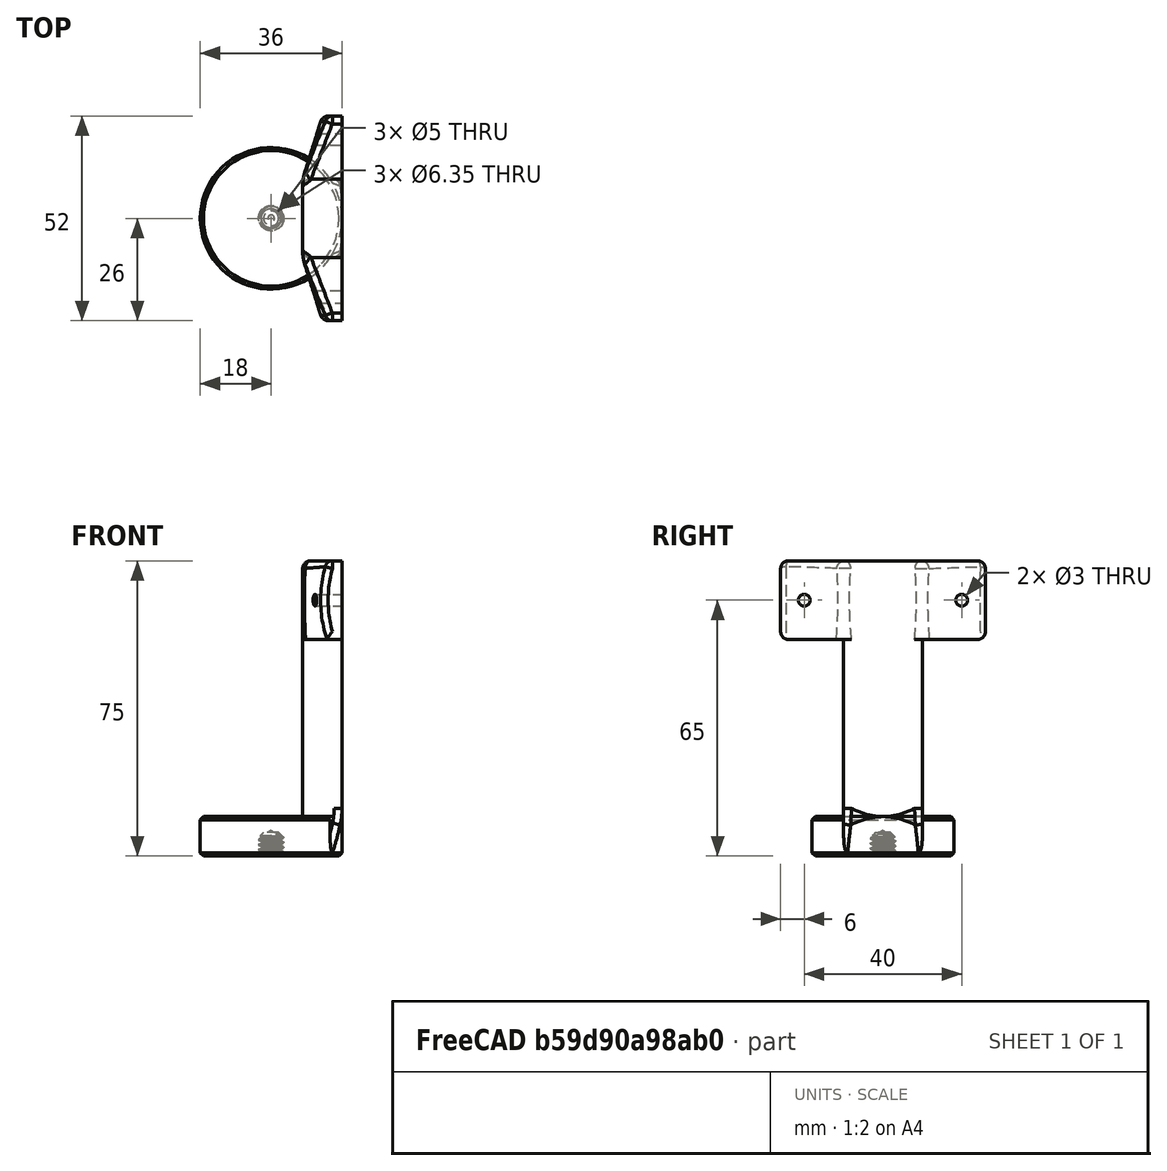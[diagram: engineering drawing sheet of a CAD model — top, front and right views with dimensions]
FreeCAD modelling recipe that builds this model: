
FCSTD DOCUMENT  (FreeCAD 0.21R33668 +7 (Git))
Label: _RaspiCam-Holder
License: Creative Commons Attribution 4.0
LicenseURL: https://creativecommons.org/licenses/by/4.0/
objects: Sketcher::SketchObject×7, PartDesign::Fillet×3, PartDesign::AdditiveLoft×2, PartDesign::Revolution×1, Part::FeaturePython×1, PartDesign::Pad×1, PartDesign::Pocket×1, PartDesign::Mirrored×1, PartDesign::Body×1, Part::Cut×1
note: 27 computed .brp shape members not serialized (recipe doc carries the construction recipe); baked Part::Feature solids carry a one-line shape summary decoded from their .brp

FEATURE [Sketcher::SketchObject] Sketch
  FullyConstrained = true
  MapMode = 5
  Placement = pos=(0,0,0) rot=(1,0,0;1.5708rad)
  Support = -> [XZ_Plane]
  sketch-geometry (8):
    g0: LineSegment StartX=0 StartY=6.50215 StartZ=0 EndX=2.5 EndY=5 EndZ=0
    g1: LineSegment StartX=2.5 StartY=5 StartZ=0 EndX=2.5 EndY=0 EndZ=0
    g2: LineSegment StartX=2.5 StartY=0 StartZ=0 EndX=17.2 EndY=0 EndZ=0
    g3: LineSegment StartX=17.2 StartY=0 StartZ=0 EndX=18 EndY=0.8 EndZ=0
    g4: LineSegment StartX=18 StartY=0.8 StartZ=0 EndX=18 EndY=9.2 EndZ=0
    g5: LineSegment StartX=18 StartY=9.2 StartZ=0 EndX=17.2 EndY=10 EndZ=0
    g6: LineSegment StartX=17.2 StartY=10 StartZ=0 EndX=0 EndY=10 EndZ=0
    g7: LineSegment StartX=0 StartY=10 StartZ=0 EndX=0 EndY=6.50215 EndZ=0
  constraints (24):
    c: PointOnObject(g0,g-2)
    c: Coincident(g0,g1)
    c: PointOnObject(g1,g-1)
    c: Vertical(g1)
    c: Coincident(g1,g2)
    c: PointOnObject(g2,g-1)
    c: Coincident(g2,g3)
    c: Coincident(g3,g4)
    c: Vertical(g4)
    c: Coincident(g4,g5)
    c: Coincident(g5,g6)
    c: PointOnObject(g6,g-2)
    c: Horizontal(g6)
    c: Coincident(g6,g7)
    c: Coincident(g0,g7)
    c: Angle(g-2,g0) = 1.02974
    c: DistanceX(g-1,g1) = 2.5
    c: DistanceY(g-1,g0) = 5
    c: DistanceX(g6,g4) = 18
    c: Vertical(g2,g5)
    c: Angle(g3,g2) = 2.35619
    c: DistanceY(g2,g3) = 0.8
    c: Perpendicular(g5,g3)
    c: DistanceY(g2,g5) = 10  'hight'
FEATURE [PartDesign::Revolution] Revolution
  Angle = 360
  Axis = (0,2e-16,1)
  Base = (0,0,0)
  Placement = pos=(0,0,0) rot=(1,0,0;1.5708rad)
  Profile = -> Sketch
  ReferenceAxis = -> Sketch [V_Axis]
  Reversed = true
FEATURE [Part::FeaturePython] ThreadedRod  label="1/4inx8-ThreadedRod"  # Fasteners workbench fastener (typed FeaturePython)
  Placement = pos=(0,0,6) rot=(0,0,1;0rad)
  diameter = 10
  diameterCustom = 6
  invert = false
  leftHanded = false
  length = 8
  matchOuter = false
  offset = 0
  pitchCustom = 1
  thread = true
  type = 5
FEATURE [Sketcher::SketchObject] Sketch001
  AttachmentOffset = pos=(0,0,10) rot=(0,0,1;0rad)
  FullyConstrained = true
  MapMode = 5
  Placement = pos=(0,0,10) rot=(0,0,1;0rad)
  Support = -> [XY_Plane]
  sketch-geometry (4):
    g0: LineSegment StartX=18 StartY=10 StartZ=0 EndX=8 EndY=10 EndZ=0
    g1: LineSegment StartX=8 StartY=10 StartZ=0 EndX=8 EndY=-10 EndZ=0
    g2: LineSegment StartX=8 StartY=-10 StartZ=0 EndX=18 EndY=-10 EndZ=0
    g3: LineSegment StartX=18 StartY=-10 StartZ=0 EndX=18 EndY=10 EndZ=0
  constraints (11):
    c: Coincident(g0,g1)
    c: Coincident(g1,g2)
    c: Coincident(g2,g3)
    c: Coincident(g3,g0)
    c: Horizontal(g0)
    c: Horizontal(g2)
    c: Vertical(g1)
    c: Symmetric(g2,g0,g-1)
    c: DistanceY(g3,g3) = 20
    c: DistanceX(g-1,g0) = 18
    c: DistanceX(g2,g2) = 10
FEATURE [Sketcher::SketchObject] Sketch002
  AttachmentOffset = pos=(0,0,0.8) rot=(0,0,1;0rad)
  ExternalGeometry = -> [Sketch001]
  FullyConstrained = true
  MapMode = 5
  Placement = pos=(0,0,0.8) rot=(0,0,1;0rad)
  Support = -> [XY_Plane]
  sketch-geometry (4):
    g0: ArcOfCircle CenterX=0 CenterY=0 CenterZ=0 NormalX=0 NormalY=0 NormalZ=1 AngleXU=0 Radius=18 StartAngle=5.69415 EndAngle=6.87222
    g1: LineSegment StartX=14.9666 StartY=-10 StartZ=0 EndX=8 EndY=-10 EndZ=0
    g2: LineSegment StartX=8 StartY=-10 StartZ=0 EndX=8 EndY=10 EndZ=0
    g3: LineSegment StartX=8 StartY=10 StartZ=0 EndX=14.9666 EndY=10 EndZ=0
  constraints (10):
    c: Coincident(g0,g-1)
    c: Coincident(g0,g1)
    c: Coincident(g1,g2)
    c: Coincident(g2,g3)
    c: Coincident(g3,g0)
    c: Horizontal(g3)
    c: Horizontal(g1)
    c: Symmetric(g1,g2,g-1)
    c: Coincident(g2,g-3)
    c: Radius(g0) = 18
FEATURE [PartDesign::AdditiveLoft] AdditiveLoft
  BaseFeature = -> Revolution
  Closed = false
  Placement = pos=(0,0,0) rot=(1,0,0;1.5708rad)
  Profile = -> Sketch001
  Ruled = false
  Sections = -> [Sketch002]
FEATURE [Sketcher::SketchObject] Sketch003
  AttachmentOffset = pos=(0,0,10) rot=(0,0,1;0rad)
  FullyConstrained = true
  MapMode = 5
  Placement = pos=(0,0,10) rot=(0,0,1;0rad)
  Support = -> [XY_Plane]
  sketch-geometry (4):
    g0: LineSegment StartX=18 StartY=10 StartZ=0 EndX=8 EndY=10 EndZ=0
    g1: LineSegment StartX=8 StartY=10 StartZ=0 EndX=8 EndY=-10 EndZ=0
    g2: LineSegment StartX=8 StartY=-10 StartZ=0 EndX=18 EndY=-10 EndZ=0
    g3: LineSegment StartX=18 StartY=-10 StartZ=0 EndX=18 EndY=10 EndZ=0
  constraints (11):
    c: Coincident(g0,g1)
    c: Coincident(g1,g2)
    c: Coincident(g2,g3)
    c: Coincident(g3,g0)
    c: Horizontal(g0)
    c: Horizontal(g2)
    c: Vertical(g1)
    c: Symmetric(g2,g0,g-1)
    c: DistanceY(g3,g3) = 20
    c: DistanceX(g-1,g0) = 18
    c: DistanceX(g2,g2) = 10
FEATURE [PartDesign::Pad] Pad
  BaseFeature = -> AdditiveLoft
  Direction = (0,0,1)
  Length = 65
  Length2 = 10
  Placement = pos=(0,0,0) rot=(1,0,0;1.5708rad)
  Profile = -> Sketch003
  ReferenceAxis = -> Sketch003 [N_Axis]
  Type = 0
FEATURE [Sketcher::SketchObject] Sketch004
  AttachmentOffset = pos=(0,0,10) rot=(0,0,1;0rad)
  ExternalGeometry = -> [Pad]
  FullyConstrained = true
  MapMode = 5
  Placement = pos=(0,-10,2.2e-15) rot=(1,0,0;1.5708rad)
  Support = -> [XZ_Plane]
  sketch-geometry (4):
    g0: LineSegment StartX=8 StartY=75 StartZ=0 EndX=18 EndY=75 EndZ=0
    g1: LineSegment StartX=18 StartY=75 StartZ=0 EndX=18 EndY=55 EndZ=0
    g2: LineSegment StartX=18 StartY=55 StartZ=0 EndX=8 EndY=55 EndZ=0
    g3: LineSegment StartX=8 StartY=55 StartZ=0 EndX=8 EndY=75 EndZ=0
  constraints (10):
    c: Coincident(g0,g1)
    c: Coincident(g1,g2)
    c: Coincident(g2,g3)
    c: Coincident(g3,g0)
    c: Horizontal(g2)
    c: Vertical(g1)
    c: Vertical(g3)
    c: Coincident(g0,g-3)
    c: Coincident(g0,g-4)
    c: DistanceY(g3,g3) = 20
FEATURE [Sketcher::SketchObject] Sketch005
  AttachmentOffset = pos=(0,0,26) rot=(0,0,1;0rad)
  ExternalGeometry = -> [Pad]
  FullyConstrained = true
  MapMode = 5
  Placement = pos=(0,-26,5.8e-15) rot=(1,0,0;1.5708rad)
  Support = -> [XZ_Plane]
  sketch-geometry (5):
    g0: LineSegment StartX=18 StartY=75 StartZ=0 EndX=18 EndY=55 EndZ=0
    g1: LineSegment StartX=18 StartY=55 StartZ=0 EndX=14.7157 EndY=55 EndZ=0
    g2: LineSegment StartX=18 StartY=75 StartZ=0 EndX=14.7157 EndY=75 EndZ=0
    g3: ArcOfCircle CenterX=43 CenterY=65 CenterZ=0 NormalX=0 NormalY=0 NormalZ=1 AngleXU=0 Radius=30 StartAngle=2.80176 EndAngle=3.48143
    g4: LineSegment StartX=13 StartY=65 StartZ=0 EndX=43 EndY=65 EndZ=0
  constraints (14):
    c: Coincident(g0,g1)
    c: Horizontal(g1)
    c: DistanceY(g1,g-3) = 20
    c: Coincident(g2,g0)
    c: Horizontal(g2)
    c: Coincident(g3,g1)
    c: Coincident(g3,g2)
    c: Coincident(g0,g-4)
    c: PointOnObject(g4,g3)
    c: Coincident(g4,g3)
    c: Horizontal(g4)
    c: Symmetric(g0,g0,g4)
    c: DistanceX(g4,g0) = 5
    c: DistanceX(g4,g4) = 30
FEATURE [PartDesign::AdditiveLoft] AdditiveLoft001
  BaseFeature = -> Pad
  Closed = false
  Placement = pos=(0,0,0) rot=(1,0,0;1.5708rad)
  Profile = -> Sketch004
  Ruled = false
  Sections = -> [Sketch005]
FEATURE [Sketcher::SketchObject] Sketch006
  AttachmentOffset = pos=(0,0,18) rot=(0,0,1;0rad)
  FullyConstrained = true
  MapMode = 5
  Placement = pos=(18,-4e-15,4e-15) rot=(0.57735,0.57735,0.57735;2.0944rad)
  Support = -> [YZ_Plane]
  sketch-geometry (1):
    g0: Circle CenterX=-20 CenterY=65 CenterZ=0 NormalX=0 NormalY=0 NormalZ=1 AngleXU=0 Radius=1.5
  constraints (3):
    c: DistanceY(g-1,g0) = 65
    c: Diameter(g0) = 3
    c: DistanceX(g0,g-1) = 20
FEATURE [PartDesign::Pocket] Pocket
  BaseFeature = -> AdditiveLoft001
  Direction = (-1,2e-16,-3e-16)
  Length = 5
  Length2 = 5
  Placement = pos=(0,0,0) rot=(1,0,0;1.5708rad)
  Profile = -> Sketch006
  ReferenceAxis = -> Sketch006 [N_Axis]
  Type = 1
FEATURE [PartDesign::Mirrored] Mirrored
  BaseFeature = -> Pocket
  MirrorPlane = -> XZ_Plane
  Originals = -> [AdditiveLoft001,Pocket]
  Placement = pos=(0,0,0) rot=(1,0,0;1.5708rad)
FEATURE [PartDesign::Fillet] Fillet
  Base = -> Mirrored [Edge11]
  BaseFeature = -> Mirrored
  Placement = pos=(0,0,0) rot=(1,0,0;1.5708rad)
  Radius = 20
  SupportTransform = false
  UseAllEdges = false
FEATURE [PartDesign::Fillet] Fillet001
  Base = -> Fillet [Edge12,Edge19,Edge27,Edge36,Edge43,Edge66,Edge68,Edge57,Edge59,Edge63,Edge58,Edge41,Edge62]
  BaseFeature = -> Fillet
  Placement = pos=(0,0,0) rot=(1,0,0;1.5708rad)
  Radius = 2
  SupportTransform = false
  UseAllEdges = false
FEATURE [PartDesign::Fillet] Fillet002
  Base = -> Fillet001 [Edge89,Edge91]
  BaseFeature = -> Fillet001
  Placement = pos=(0,0,0) rot=(1,0,0;1.5708rad)
  Radius = 9.9
  SupportTransform = false
  UseAllEdges = false
FEATURE [PartDesign::Body] Body
  Group = -> [Revolution,Sketch,Sketch001,Sketch002,AdditiveLoft,Sketch003,Pad,Sketch004,Sketch005,AdditiveLoft001,Sketch006,Pocket,Mirrored,Fillet,Fillet001,Fillet002]
  Origin = -> Origin
  Tip = -> Fillet002
FEATURE [Part::Cut] Cut  label="RaspiCam-Holder"
  Base = -> Body
  Tool = -> ThreadedRod
